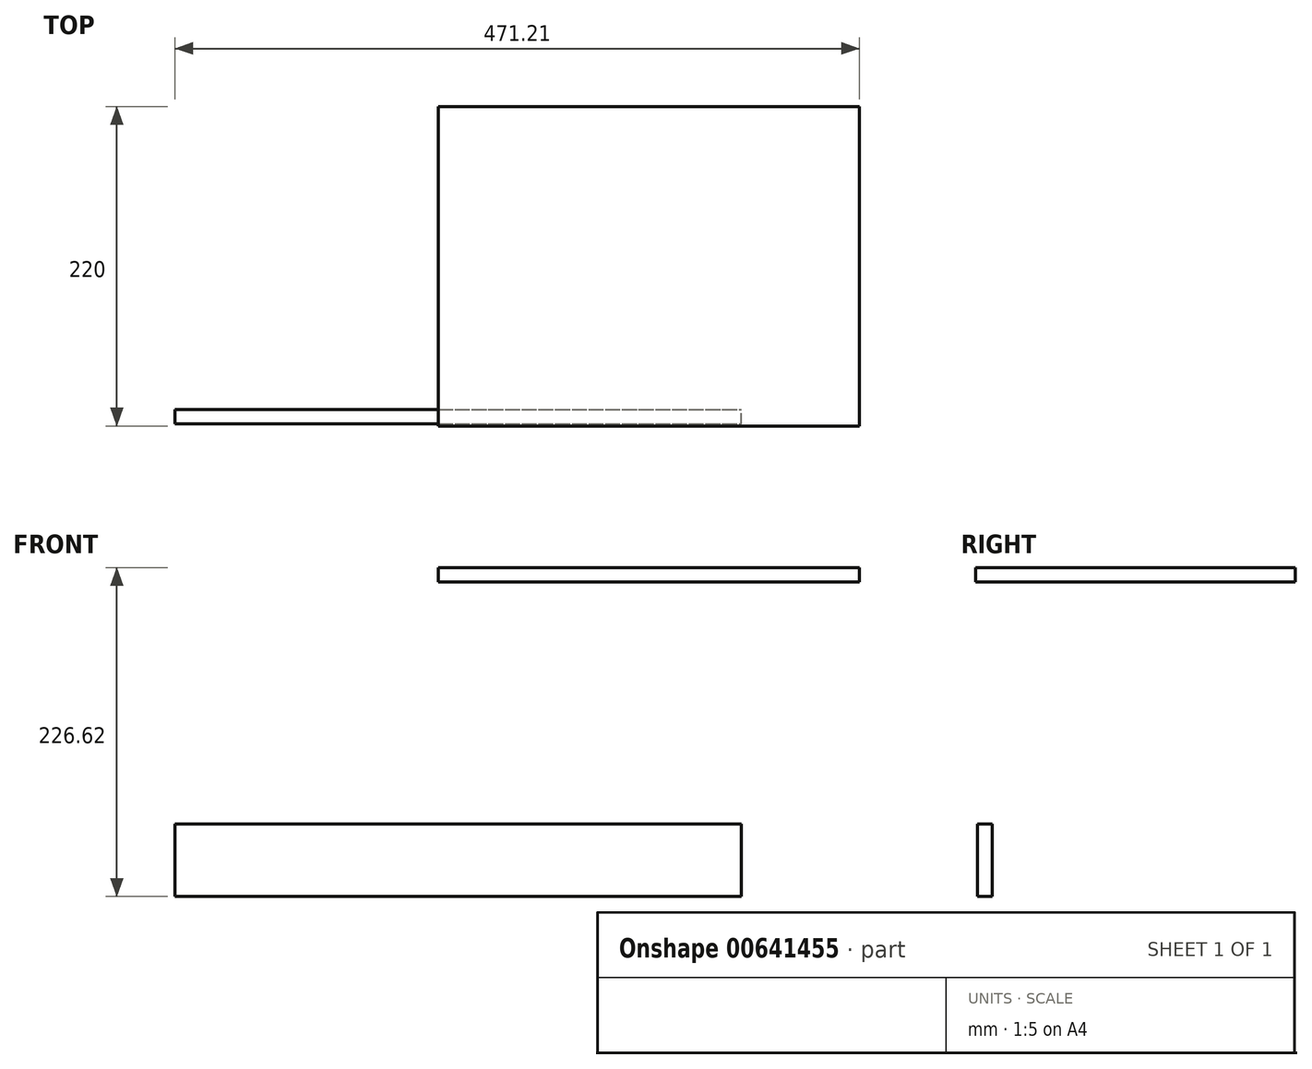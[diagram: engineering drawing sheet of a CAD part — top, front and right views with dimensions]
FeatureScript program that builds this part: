
annotation { "Feature Type Name" : "Feature", "Feature Type Description" : "" }
export const myFeature = defineFeature(function(context is Context, id is Id, definition is map)
    precondition{}
    {
        {
            var Q0;
            Q0=qCreatedBy(makeId("Top.planeOp"),FACE);
            var sketch = newSketch(context, id + "F0", { "sketchPlane" : qUnion([Q0])});
            skLineSegment(sketch, "E0.bottom", {"start": v(-1064.38, 465.67) * mm, "end": v(-277.5, 465.67) * mm});
            skLineSegment(sketch, "E0.top", {"start": v(-1064.38, -93.13) * mm, "end": v(-277.5, -93.13) * mm});
            skLineSegment(sketch, "E0.left", {"start": v(-1064.38, 465.67) * mm, "end": v(-1064.38, -93.13) * mm});
            skLineSegment(sketch, "E0.right", {"start": v(-277.5, 465.67) * mm, "end": v(-277.5, -93.13) * mm});
            skLineSegment(sketch, "E1.bottom", {"start": v(-802.09, 579.7) * mm, "end": v(0, 579.7) * mm});
            skLineSegment(sketch, "E1.top", {"start": v(-802.09, 982.65) * mm, "end": v(0, 982.65) * mm});
            skLineSegment(sketch, "E1.left", {"start": v(-802.09, 579.7) * mm, "end": v(-802.09, 982.65) * mm});
            skLineSegment(sketch, "E1.right", {"start": v(0, 579.7) * mm, "end": v(0, 982.65) * mm});
            skLineSegment(sketch, "E2.bottom", {"start": v(-144.94, 208.66) * mm, "end": v(145.06, 208.66) * mm});
            skLineSegment(sketch, "E2.top", {"start": v(-144.94, -11.34) * mm, "end": v(145.06, -11.34) * mm});
            skLineSegment(sketch, "E2.left", {"start": v(-144.94, 208.66) * mm, "end": v(-144.94, -11.34) * mm});
            skLineSegment(sketch, "E2.right", {"start": v(145.06, 208.66) * mm, "end": v(145.06, -11.34) * mm});
            skSolve(sketch);
        }
        {
            var Q0;
            Q0=makeQuery(id+"F0.imprint","IMPRINT",FACE,{"disambiguationData":[TD([[makeQuery(id+"F0.imprint","IMPRINT",EDGE,{"derivedFrom":sQuery(id+"F0.wireOp",EDGE,"E2.bottom")}),-1.0]])]});
            extrude(context, id + "F1", {"entities" : qUnion([Q0]), "depth" : 10 * mm, "offsetDistance" : 25 * mm});
        }
        {
            var Q0;
            Q0=qCreatedBy(makeId("Front.planeOp"),FACE);
            var sketch = newSketch(context, id + "F2", { "sketchPlane" : qUnion([Q0])});
            skLineSegment(sketch, "E3.bottom", {"start": v(-326.15, -166.62) * mm, "end": v(63.85, -166.62) * mm});
            skLineSegment(sketch, "E3.top", {"start": v(-326.15, -216.62) * mm, "end": v(63.85, -216.62) * mm});
            skLineSegment(sketch, "E3.left", {"start": v(-326.15, -166.62) * mm, "end": v(-326.15, -216.62) * mm});
            skLineSegment(sketch, "E3.right", {"start": v(63.85, -166.62) * mm, "end": v(63.85, -216.62) * mm});
            skSolve(sketch);
        }
        {
            var Q0;
            Q0=makeQuery(id+"F2.imprint","IMPRINT",FACE,{"disambiguationData":[TD([[makeQuery(id+"F2.imprint","IMPRINT",EDGE,{"derivedFrom":sQuery(id+"F2.wireOp",EDGE,"E3.bottom")}),-1.0]])]});
            extrude(context, id + "F3", {"entities" : qUnion([Q0]), "depth" : 10 * mm, "offsetDistance" : 25 * mm});
        }
    });
